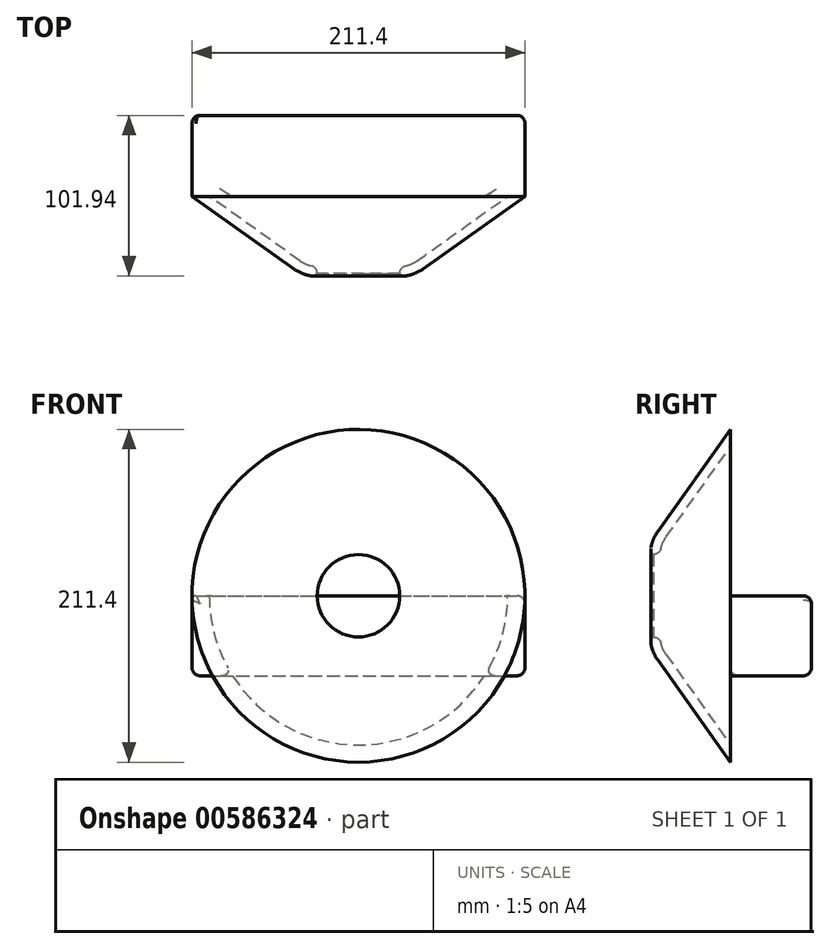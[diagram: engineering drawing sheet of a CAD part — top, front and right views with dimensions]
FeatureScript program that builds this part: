
annotation { "Feature Type Name" : "Feature", "Feature Type Description" : "" }
export const myFeature = defineFeature(function(context is Context, id is Id, definition is map)
    precondition{}
    {
        {
            var Q0;
            Q0=qCreatedBy(makeId("Top.planeOp"),FACE);
            var sketch = newSketch(context, id + "F0", { "sketchPlane" : qUnion([Q0])});
            skLineSegment(sketch, "E0.bottom", {"start": v(-105.7, 25.73) * mm, "end": v(105.7, 25.73) * mm});
            skLineSegment(sketch, "E0.top", {"start": v(-105.7, -25.73) * mm, "end": v(105.7, -25.73) * mm});
            skLineSegment(sketch, "E0.left", {"start": v(-105.7, 25.73) * mm, "end": v(-105.7, -25.73) * mm});
            skLineSegment(sketch, "E0.right", {"start": v(105.7, 25.73) * mm, "end": v(105.7, -25.73) * mm});
            skPoint(sketch, "E0.middle", {"position": v(0, 0) * mm});
            skSolve(sketch);
        }
        {
            var Q0;
            Q0 = qSketchRegion(id + "F0", true);
            extrude(context, id + "F1", {"entities" : qUnion([Q0]), "endBound" : BoundingType.SYMMETRIC, "depth" : 50.8 * mm, "offsetDistance" : 25.4 * mm});
        }
        {
            var Q0;
            Q0=makeQuery(id+"F1.opExtrude","CAP_FACE",FACE,{"disambiguationData":[OSD([sQuery(id+"F0.wireOp",EDGE,"E0.bottom"),sQuery(id+"F0.wireOp",EDGE,"E0.top"),sQuery(id+"F0.wireOp",EDGE,"E0.left"),sQuery(id+"F0.wireOp",EDGE,"E0.right")])],"isStart":false});
            var sketch = newSketch(context, id + "F2", { "sketchPlane" : qUnion([Q0])});
            skLineSegment(sketch, "E1", {"start": v(0, -76.53) * mm, "end": v(26.18, -76.53) * mm});
            skLineSegment(sketch, "E2", {"start": v(40.9, -71.83) * mm, "end": v(105.7, -25.73) * mm});
            skLineSegment(sketch, "E3", {"start": v(0, -76.53) * mm, "end": v(0, -25.73) * mm, "construction": true});
            skPoint(sketch, "E4.visualSharp", {"position": v(-34.3, -76.53) * mm});
            skPoint(sketch, "E5.visualSharp", {"position": v(34.3, -76.53) * mm});
            skArc(sketch, "E5.filletArc", {"start": v(26.18, -76.53) * mm, "mid": v(33.91, -75.33) * mm, "end": v(40.9, -71.83) * mm});
            skLineSegment(sketch, "E6.0", {"start": v(37.23, -66.66) * mm, "end": v(94.74, -25.73) * mm});
            skLineSegment(sketch, "E6.3", {"start": v(0, -70.18) * mm, "end": v(26.18, -70.18) * mm});
            skArc(sketch, "E6.4", {"start": v(26.18, -70.18) * mm, "mid": v(31.98, -69.28) * mm, "end": v(37.23, -66.66) * mm});
            skLineSegment(sketch, "E7", {"start": v(0, -70.18) * mm, "end": v(0, -76.53) * mm});
            skSolve(sketch);
        }
        {
            var Q0;
            Q0=makeQuery(id+"F2.imprint","IMPRINT",FACE,{"disambiguationData":[TD([[makeQuery(id+"F2.imprint","IMPRINT",EDGE,{"derivedFrom":sQuery(id+"F2.wireOp",EDGE,"E1")}),1.0]])]});
            var Q1;
            Q1=sQuery(id+"F2.wireOp",EDGE,"E3");
            revolve(context, id + "F3", {"operationType" : NewBodyOperationType.ADD, "entities" : qUnion([Q0]), "axis" : qUnion([Q1]), "revolveType" : RevolveType.FULL});
        }
        {
            var Q0;
            Q0=makeQuery(id+"F3.opRevolve","SWEPT_FACE",FACE,{"disambiguationData":[OSD([sQuery(id+"F2.wireOp",EDGE,"E6.3")])]});
            extrude(context, id + "F4", {"entities" : qUnion([Q0]), "operationType" : NewBodyOperationType.REMOVE, "oppositeDirection" : true, "depth" : 6.35 * mm, "offsetDistance" : 25.4 * mm});
        }
        {
            var Q0;
            Q0=makeQuery(id+"F1.opExtrude","CAP_EDGE",EDGE,{"disambiguationData":[OSD([sQuery(id+"F0.wireOp",EDGE,"E0.left")])],"isStart":false});
            fillet(context, id + "F5", {"entities" : qUnion([Q0]), "radius" : 2.54 * mm, "tangentPropagation" : true, "allowEdgeOverflow" : false});
        }
        {
            var Q0;
            Q0=makeQuery(id+"F1.opExtrude","CAP_EDGE",EDGE,{"disambiguationData":[OSD([sQuery(id+"F0.wireOp",EDGE,"E0.right")])],"isStart":false});
            fillet(context, id + "F6", {"entities" : qUnion([Q0]), "radius" : 5.08 * mm, "tangentPropagation" : true, "allowEdgeOverflow" : false});
        }
        {
            var Q0;
            Q0=makeQuery(id+"F1.opExtrude","CAP_EDGE",EDGE,{"disambiguationData":[OSD([sQuery(id+"F0.wireOp",EDGE,"E0.left")])],"isStart":true});
            fillet(context, id + "F7", {"entities" : qUnion([Q0]), "radius" : 5.08 * mm, "tangentPropagation" : true, "allowEdgeOverflow" : false});
        }
        {
            var Q0;
            Q0=makeQuery(id+"F1.opExtrude","CAP_EDGE",EDGE,{"disambiguationData":[OSD([sQuery(id+"F0.wireOp",EDGE,"E0.right")])],"isStart":true});
            var Q1;
            {var subQ0=sQuery(id+"F0.wireOp",EDGE,"E0.top");var subQ1=sQuery(id+"F2.wireOp",EDGE,"E6.0");var subQ2=makeQuery(id+"F3.opRevolve","SWEPT_FACE",FACE,{"disambiguationData":[OSD([subQ1])]});var subQ3=makeQuery(id+"F3.opRevolve","SWEPT_FACE",FACE,{"disambiguationData":[OSD([subQ0])]});Q1=makeQuery(id+"F3.boolean.opBoolean","SPLIT",EDGE,{"disambiguationData":[topologyDisambiguationEdgeConnected([subQ2,subQ3]),TD([makeQuery(id+"F1.opExtrude","CAP_FACE",FACE,{"disambiguationData":[OSD([sQuery(id+"F0.wireOp",EDGE,"E0.bottom"),subQ0,sQuery(id+"F0.wireOp",EDGE,"E0.left"),sQuery(id+"F0.wireOp",EDGE,"E0.right")])],"isStart":false})])],"derivedFrom":makeQuery(id+"F3.opRevolve","SWEPT_EDGE",EDGE,{"disambiguationData":[OSD([subQ0,subQ1])]})});}
            fillet(context, id + "F8", {"entities" : qUnion([Q0, Q1]), "radius" : 5.08 * mm, "tangentPropagation" : true, "allowEdgeOverflow" : false});
        }
        {
            var Q0;
            {var subQ0=sQuery(id+"F2.wireOp",EDGE,"E6.4");var subQ1=sQuery(id+"F2.wireOp",EDGE,"E6.3");Q0=makeQuery(id+"F4.boolean.opBoolean","MERGE",EDGE,{"derivedFrom":[makeQuery(id+"F3.opRevolve","SWEPT_EDGE",EDGE,{"disambiguationData":[OSD([subQ1,subQ0])]}),makeQuery(id+"F4.opExtrude","CAP_EDGE",EDGE,{"disambiguationData":[OSD([subQ1,subQ0])],"isStart":true})]});}
            fillet(context, id + "F9", {"entities" : qUnion([Q0]), "radius" : 5.08 * mm, "tangentPropagation" : true, "allowEdgeOverflow" : false});
        }
        {
            var Q0;
            Q0=makeQuery(id+"F4.boolean.opBoolean","MERGE",EDGE,{"derivedFrom":[makeQuery(id+"F3.opRevolve","SWEPT_EDGE",EDGE,{"disambiguationData":[OSD([sQuery(id+"F2.wireOp",EDGE,"E1"),sQuery(id+"F2.wireOp",EDGE,"E5.filletArc")])]}),makeQuery(id+"F4.opExtrude","CAP_EDGE",EDGE,{"disambiguationData":[OSD([sQuery(id+"F2.wireOp",EDGE,"E6.3"),sQuery(id+"F2.wireOp",EDGE,"E6.4")])],"isStart":false})]});
            fillet(context, id + "F10", {"entities" : qUnion([Q0]), "radius" : 5.08 * mm, "tangentPropagation" : true, "allowEdgeOverflow" : false});
        }
        {
            var Q0;
            Q0=makeQuery(id+"F1.opExtrude","CAP_EDGE",EDGE,{"disambiguationData":[OSD([sQuery(id+"F0.wireOp",EDGE,"E0.bottom")])],"isStart":true});
            var Q1;
            Q1=makeQuery(id+"F1.opExtrude","CAP_EDGE",EDGE,{"disambiguationData":[OSD([sQuery(id+"F0.wireOp",EDGE,"E0.bottom")])],"isStart":false});
            fillet(context, id + "F11", {"entities" : qUnion([Q0, Q1]), "radius" : 5.08 * mm, "tangentPropagation" : true, "allowEdgeOverflow" : false});
        }
        {
            var Q0;
            {var subQ0=sQuery(id+"F0.wireOp",EDGE,"E0.top");var subQ1=makeQuery(id+"F1.opExtrude","CAP_FACE",FACE,{"disambiguationData":[OSD([sQuery(id+"F0.wireOp",EDGE,"E0.bottom"),subQ0,sQuery(id+"F0.wireOp",EDGE,"E0.left"),sQuery(id+"F0.wireOp",EDGE,"E0.right")])],"isStart":true});var subQ2=makeQuery(id+"F1.opExtrude","SWEPT_FACE",FACE,{"disambiguationData":[OSD([subQ0])]});Q0=makeQuery(id+"F3.boolean.opBoolean","SPLIT",EDGE,{"disambiguationData":[topologyDisambiguationEdgeConnected([subQ1,subQ2]),TD([makeQuery(id+"F3.opRevolve","SWEPT_FACE",FACE,{"disambiguationData":[OSD([sQuery(id+"F2.wireOp",EDGE,"E6.0")])]})])],"derivedFrom":makeQuery(id+"F1.opExtrude","CAP_EDGE",EDGE,{"disambiguationData":[OSD([subQ0])],"isStart":true})});}
            fillet(context, id + "F12", {"entities" : qUnion([Q0]), "radius" : 5.08 * mm, "tangentPropagation" : true, "allowEdgeOverflow" : false});
        }
    });
